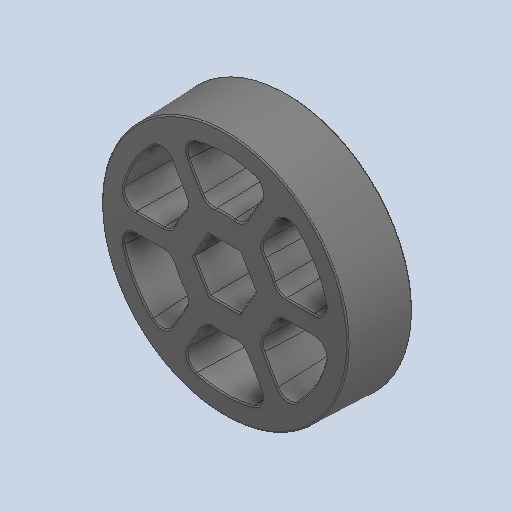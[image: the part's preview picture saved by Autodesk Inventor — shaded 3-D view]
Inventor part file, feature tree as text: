
AUTODESK INVENTOR PART (.ipt)
format: ipt  version: 2024 (Build 280153000, 153)  size: 820,224 bytes
history: native  units: in
note: dims shown in document units (in); Inventor stores cm internally (conversion verified against a paired STEP export)
features: fillet x1
ambient origin geometry x8: Origin, YZ Plane, XZ Plane, XY Plane, X Axis, Y Axis, Z Axis, Center Point
bodies: Solid1 (feature_tree)
feature tree (1):
  fillet  "Fillet3"  [1 undecoded]
note: 1 required parameter value undecoded (feature->parameter linkage not recoverable at this tier; creation-order binding heuristic only, values carry confidence <= 0.55)
